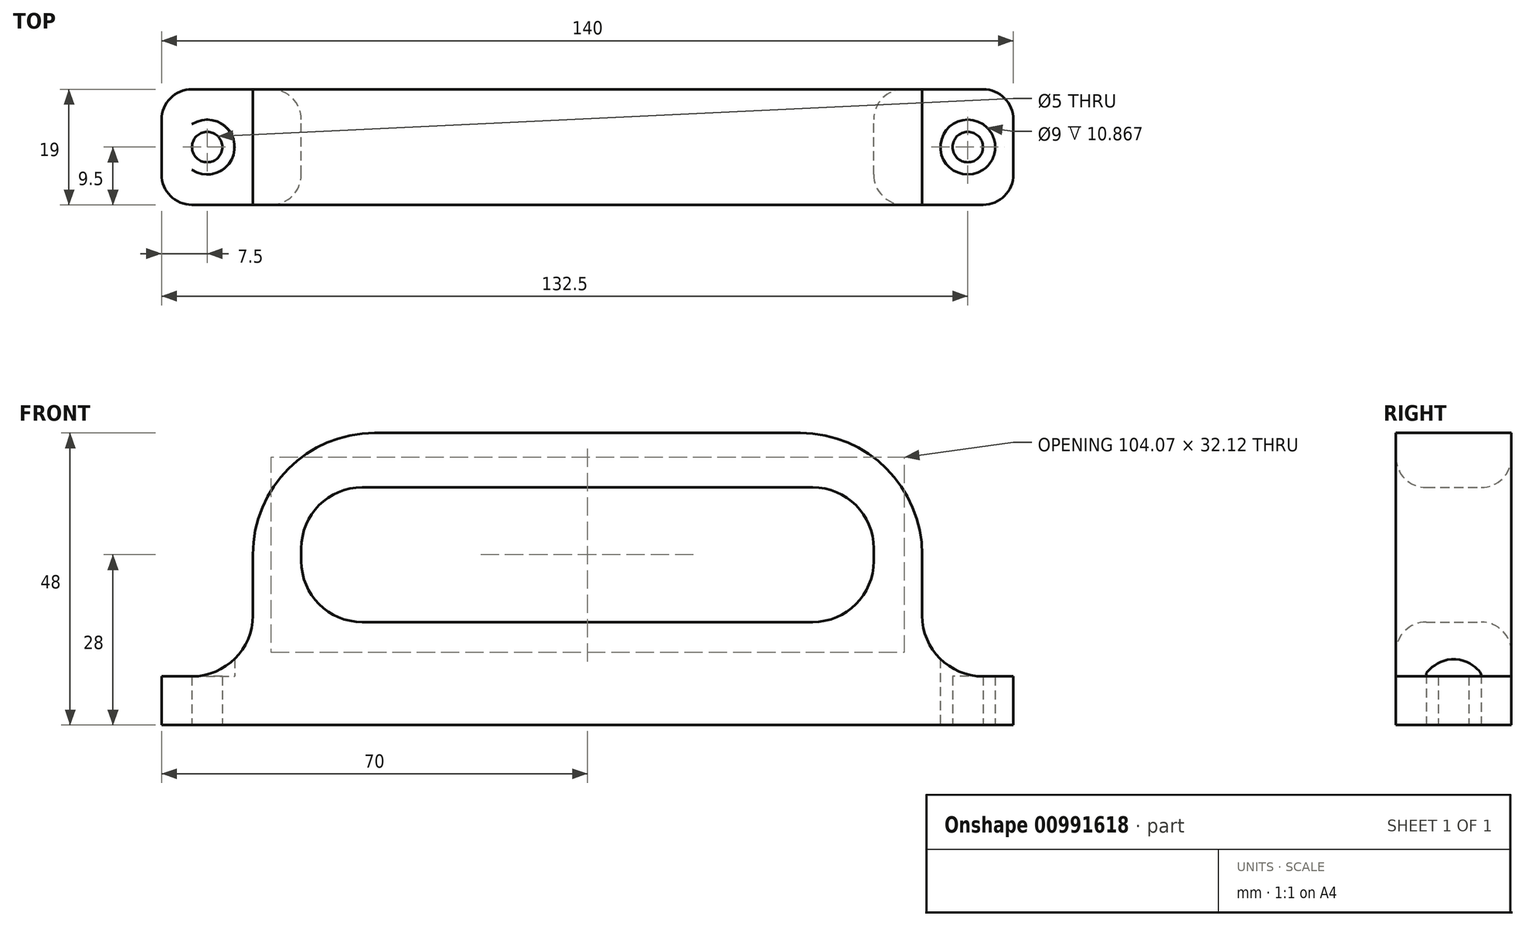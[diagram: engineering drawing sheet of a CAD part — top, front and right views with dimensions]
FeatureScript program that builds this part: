
annotation { "Feature Type Name" : "Feature", "Feature Type Description" : "" }
export const myFeature = defineFeature(function(context is Context, id is Id, definition is map)
    precondition{}
    {
        {
            var Q0;
            Q0=qCreatedBy(makeId("Front.planeOp"),FACE);
            var sketch = newSketch(context, id + "F0", { "sketchPlane" : qUnion([Q0])});
            skLineSegment(sketch, "E0.bottom", {"start": v(-70, 0) * mm, "end": v(70, 0) * mm});
            skLineSegment(sketch, "E0.top", {"start": v(-70, 8) * mm, "end": v(-65, 8) * mm});
            skLineSegment(sketch, "E0.left", {"start": v(-70, 0) * mm, "end": v(-70, 8) * mm});
            skLineSegment(sketch, "E0.right", {"start": v(70, 0) * mm, "end": v(70, 8) * mm});
            skLineSegment(sketch, "E1.top", {"start": v(35, 48) * mm, "end": v(-35, 48) * mm});
            skLineSegment(sketch, "E1.left", {"start": v(55, 8) * mm, "end": v(55, 8) * mm});
            skLineSegment(sketch, "E1.right", {"start": v(-55, 18) * mm, "end": v(-55, 28) * mm});
            skPoint(sketch, "E1.middle", {"position": v(0, 28) * mm});
            skPoint(sketch, "E2.visualSharp", {"position": v(-55, 48) * mm});
            skArc(sketch, "E2.filletArc", {"start": v(-35, 48) * mm, "mid": v(-49.14, 42.14) * mm, "end": v(-55, 28) * mm});
            skPoint(sketch, "E3.visualSharp", {"position": v(55, 48) * mm});
            skArc(sketch, "E3.filletArc", {"start": v(55, 28) * mm, "mid": v(49.14, 42.14) * mm, "end": v(35, 48) * mm});
            skLineSegment(sketch, "E4", {"start": v(65, 8) * mm, "end": v(70, 8) * mm});
            skLineSegment(sketch, "E5", {"start": v(55, 18) * mm, "end": v(55, 28) * mm});
            skPoint(sketch, "E6.visualSharp", {"position": v(-55, 8) * mm});
            skArc(sketch, "E6.filletArc", {"start": v(-65, 8) * mm, "mid": v(-57.93, 10.93) * mm, "end": v(-55, 18) * mm});
            skArc(sketch, "E7.filletArc", {"start": v(55, 18) * mm, "mid": v(57.93, 10.93) * mm, "end": v(65, 8) * mm});
            skLineSegment(sketch, "E8.bottom", {"start": v(37.04, 16.94) * mm, "end": v(-37.04, 16.94) * mm});
            skLineSegment(sketch, "E8.top", {"start": v(37.04, 39.06) * mm, "end": v(-37.04, 39.06) * mm});
            skLineSegment(sketch, "E8.left", {"start": v(47.04, 26.94) * mm, "end": v(47.04, 29.06) * mm});
            skLineSegment(sketch, "E8.right", {"start": v(-47.04, 26.94) * mm, "end": v(-47.04, 29.06) * mm});
            skPoint(sketch, "E9.visualSharp", {"position": v(47.04, 39.06) * mm});
            skArc(sketch, "E9.filletArc", {"start": v(47.04, 29.06) * mm, "mid": v(44.1, 36.13) * mm, "end": v(37.04, 39.06) * mm});
            skPoint(sketch, "E10.visualSharp", {"position": v(47.04, 16.94) * mm});
            skArc(sketch, "E10.filletArc", {"start": v(37.04, 16.94) * mm, "mid": v(44.1, 19.87) * mm, "end": v(47.04, 26.94) * mm});
            skPoint(sketch, "E11.visualSharp", {"position": v(-47.04, 16.94) * mm});
            skArc(sketch, "E11.filletArc", {"start": v(-47.04, 26.94) * mm, "mid": v(-44.1, 19.87) * mm, "end": v(-37.04, 16.94) * mm});
            skPoint(sketch, "E12.visualSharp", {"position": v(-47.04, 39.06) * mm});
            skArc(sketch, "E12.filletArc", {"start": v(-37.04, 39.06) * mm, "mid": v(-44.1, 36.13) * mm, "end": v(-47.04, 29.06) * mm});
            skSolve(sketch);
        }
        {
            var Q0;
            Q0=makeQuery(id+"F0.imprint","IMPRINT",FACE,{"disambiguationData":[TD([[makeQuery(id+"F0.imprint","IMPRINT",EDGE,{"derivedFrom":sQuery(id+"F0.wireOp",EDGE,"E0.bottom")}),1.0]])]});
            extrude(context, id + "F1", {"entities" : qUnion([Q0]), "depth" : 19 * mm, "offsetDistance" : 25.4 * mm});
        }
        {
            var Q0;
            Q0=qCreatedBy(makeId("Top.planeOp"),FACE);
            var sketch = newSketch(context, id + "F2", { "sketchPlane" : qUnion([Q0])});
            skCircle(sketch, "E13", {"center": v(-62.5, -9.5) * mm, "radius": 2.5 * mm});
            skCircle(sketch, "E14", {"center": v(-62.5, -9.5) * mm, "radius": 4.5 * mm});
            skCircle(sketch, "E15.MirrorC", {"center": v(62.5, -9.5) * mm, "radius": 2.5 * mm});
            skCircle(sketch, "E16.MirrorC", {"center": v(62.5, -9.5) * mm, "radius": 4.5 * mm});
            skSolve(sketch);
        }
        {
            var Q0;
            Q0=makeQuery(id+"F2.imprint","IMPRINT",FACE,{"disambiguationData":[TD([[makeQuery(id+"F2.imprint","IMPRINT",EDGE,{"derivedFrom":sQuery(id+"F2.wireOp",EDGE,"E13")}),1.0]])]});
            var Q1;
            Q1=makeQuery(id+"F2.imprint","IMPRINT",FACE,{"disambiguationData":[TD([[makeQuery(id+"F2.imprint","IMPRINT",EDGE,{"derivedFrom":sQuery(id+"F2.wireOp",EDGE,"E15.MirrorC")}),-1.0]])]});
            var Q2;
            Q2=sQuery(id+"F2.wireOp",EDGE,"E13");
            var Q3;
            Q3=sQuery(id+"F2.wireOp",EDGE,"E15.MirrorC");
            extrude(context, id + "F3", {"entities" : qUnion([Q0, Q1]), "operationType" : NewBodyOperationType.REMOVE, "surfaceEntities" : qUnion([Q2, Q3]), "endBound" : BoundingType.THROUGH_ALL, "depth" : 25.4 * mm, "offsetDistance" : 25.4 * mm});
        }
        {
            var Q0;
            Q0=makeQuery(id+"F2.imprint","IMPRINT",FACE,{"disambiguationData":[TD([[makeQuery(id+"F2.imprint","IMPRINT",EDGE,{"derivedFrom":sQuery(id+"F2.wireOp",EDGE,"E13")}),-1.0]])]});
            var Q1;
            Q1=makeQuery(id+"F2.imprint","IMPRINT",FACE,{"disambiguationData":[TD([[makeQuery(id+"F2.imprint","IMPRINT",EDGE,{"derivedFrom":sQuery(id+"F2.wireOp",EDGE,"E15.MirrorC")}),1.0]])]});
            var Q2;
            Q2=makeQuery(id+"F1.opExtrude","SWEPT_FACE",FACE,{"disambiguationData":[OSD([sQuery(id+"F0.wireOp",EDGE,"E0.top")])]});
            var Q3;
            Q3=makeQuery(id+"F1.opExtrude","SWEPT_FACE",FACE,{"disambiguationData":[OSD([sQuery(id+"F0.wireOp",EDGE,"E4")])]});
            extrude(context, id + "F4", {"entities" : qUnion([Q0, Q1]), "operationType" : NewBodyOperationType.REMOVE, "endBound" : BoundingType.THROUGH_ALL, "depth" : 25.4 * mm, "endBoundEntityFace" : qUnion([Q2]), "offsetDistance" : 8 * mm, "hasSecondDirection" : true, "secondDirectionBound" : SecondDirectionBoundingType.UP_TO_SURFACE, "secondDirectionOppositeDirection" : false, "secondDirectionDepth" : 8 * mm, "secondDirectionBoundEntityFace" : qUnion([Q3])});
        }
        {
            var Q0;
            Q0=makeQuery(id+"F1.opExtrude","CAP_EDGE",EDGE,{"disambiguationData":[OSD([sQuery(id+"F0.wireOp",EDGE,"E8.bottom")])],"isStart":false});
            var Q1;
            Q1=makeQuery(id+"F1.opExtrude","CAP_EDGE",EDGE,{"disambiguationData":[OSD([sQuery(id+"F0.wireOp",EDGE,"E8.bottom")])],"isStart":true});
            fillet(context, id + "F5", {"entities" : qUnion([Q0, Q1]), "radius" : 5 * mm, "tangentPropagation" : true, "allowEdgeOverflow" : false});
        }
        {
            var Q0;
            Q0=makeQuery(id+"F1.opExtrude","CAP_EDGE",EDGE,{"disambiguationData":[OSD([sQuery(id+"F0.wireOp",EDGE,"E0.right")])],"isStart":false});
            var Q1;
            Q1=makeQuery(id+"F1.opExtrude","CAP_EDGE",EDGE,{"disambiguationData":[OSD([sQuery(id+"F0.wireOp",EDGE,"E0.right")])],"isStart":true});
            var Q2;
            Q2=makeQuery(id+"F1.opExtrude","CAP_EDGE",EDGE,{"disambiguationData":[OSD([sQuery(id+"F0.wireOp",EDGE,"E0.left")])],"isStart":false});
            var Q3;
            Q3=makeQuery(id+"F1.opExtrude","CAP_EDGE",EDGE,{"disambiguationData":[OSD([sQuery(id+"F0.wireOp",EDGE,"E0.left")])],"isStart":true});
            fillet(context, id + "F6", {"entities" : qUnion([Q0, Q1, Q2, Q3]), "radius" : 5 * mm, "allowEdgeOverflow" : false});
        }
    });
